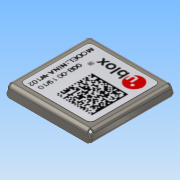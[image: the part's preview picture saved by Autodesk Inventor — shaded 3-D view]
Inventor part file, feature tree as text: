
AUTODESK INVENTOR PART (.ipt)
format: ipt  version: 2016 (Build 200138000, 138)  size: 335,360 bytes
history: native  units: mm
features: sheet_metal_op x11, other x6, sketch x6, projected_geometry x3, plane x1, mirror x1, extrude x1
ambient origin geometry x8: Origin, YZ Plane, XZ Plane, XY Plane, X Axis, Y Axis, Z Axis, Center Point
bodies: Body1 (feature_tree)
feature tree (29):
  sheet_metal_op  "Face1"
  sheet_metal_op  "Flange1"
  sheet_metal_op  "Flange2"
  plane  "Work Plane1"
  sheet_metal_op  "Face2"
  mirror  "Mirror1"
  sheet_metal_op  "Bend6"
  sheet_metal_op  "Bend7"
  extrude  "Extrusion4"  Depth=9.6mm
  other  "Decal1"
  sketch  "Sketch10"  dims[d7=9.0mm d8=9.6mm]
  other  "Plate1"
  sketch  "Sketch11"  dims[d9=0.2mm]
  other  "Plate2"
  sheet_metal_op  "Bend1"
  sheet_metal_op  "Corner1"
  sketch  "Sketch12"  dims[d10=0.2mm]
  other  "Plate3"
  sheet_metal_op  "Bend2"
  sheet_metal_op  "Corner2"
  sketch  "Sketch16"  dims[d11=0.1mm]
  other  "Plate6"
  sheet_metal_op  "Bend5"
  projected_geometry  "Projected Loop4"
  sketch  "Sketch18"  dims[d12=0.4mm]
  projected_geometry  "Projected Loop5"
  sketch  "Sketch19"  dims[d13=0.2mm d14=1.4mm d15=90.0deg d16=0.2mm d17=0.8mm d18=0.2mm d19=0.2mm d20=0.2mm d21=0.1mm d22=0.4mm d23=0.2mm d24=1.0mm d25=90.0deg d26=0.2mm d27=0.8mm d28=0.2mm d29=0.2mm d53=0.2mm d54=0.2mm d55=0.1mm d56=0.4mm d57=0.2mm d58=0.05mm d60=0.2mm d63=0.2mm d64=0.1mm d65=0.4mm d66=0.2mm d67=0.2mm d69=0.08mm d70=0.2mm d71=0.1mm d72=0.4mm d73=0.2mm d74=0.2mm d75=0.5mm d76=8.0mm d77=0.05mm d78=0.0mm]
  projected_geometry  "Projected Loop6"
  other  "Image2"
